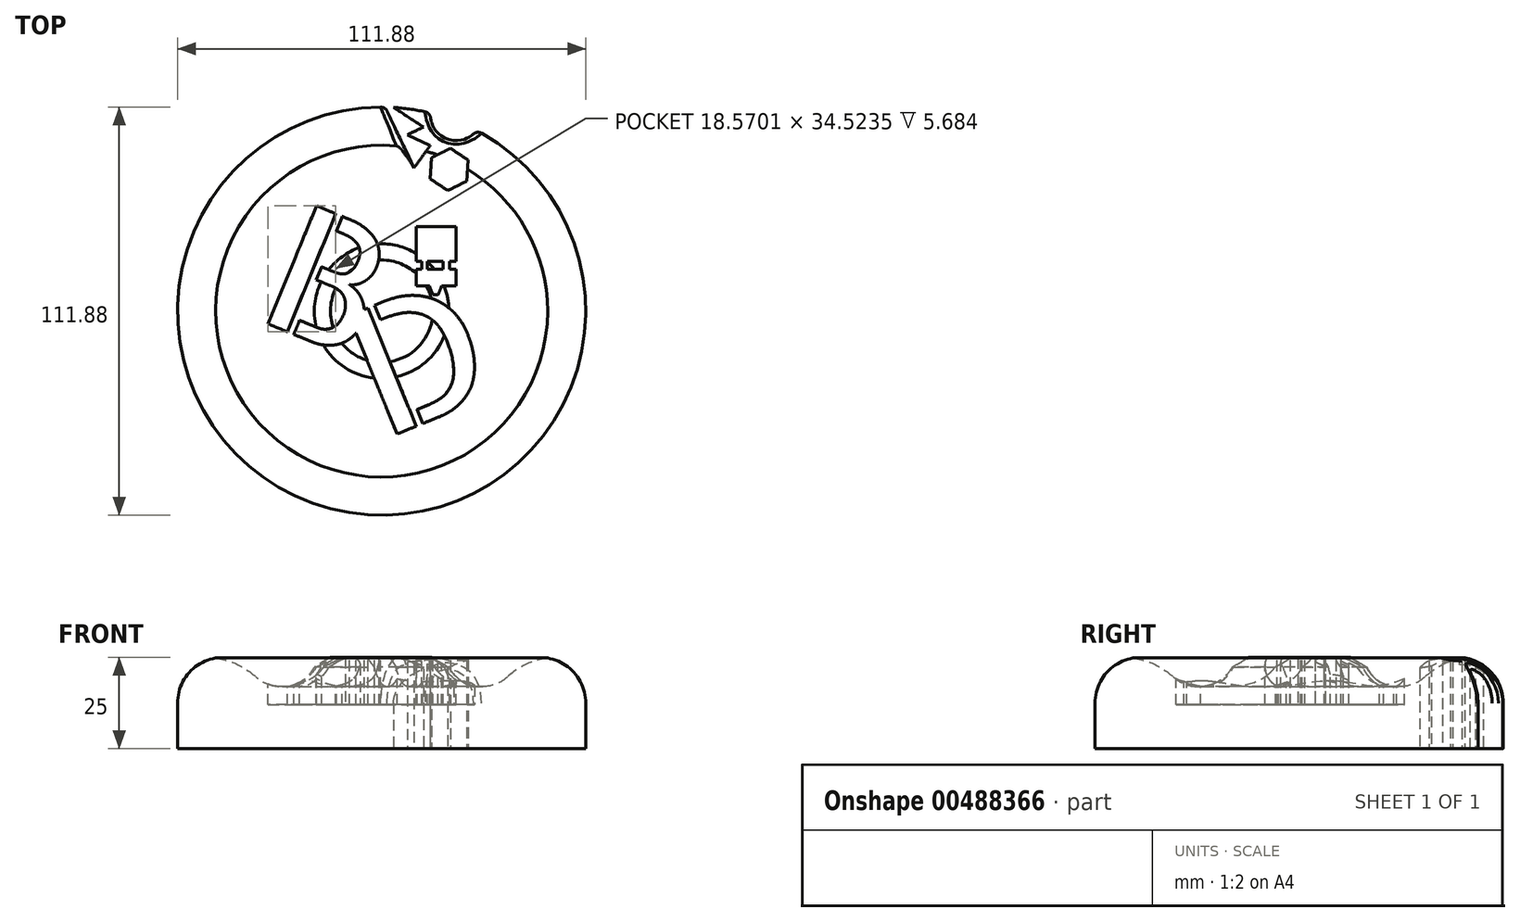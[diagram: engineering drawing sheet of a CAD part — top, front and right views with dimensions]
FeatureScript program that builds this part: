
annotation { "Feature Type Name" : "Feature", "Feature Type Description" : "" }
export const myFeature = defineFeature(function(context is Context, id is Id, definition is map)
    precondition{}
    {
        {
            var Q0;
            Q0=qCreatedBy(makeId("Top.planeOp"),FACE);
            var sketch = newSketch(context, id + "F0", { "sketchPlane" : qUnion([Q0])});
            skCircle(sketch, "E0", {"center": v(0, 0) * mm, "radius": 55.94 * mm});
            skSolve(sketch);
        }
        {
            var Q0;
            Q0 = qSketchRegion(id + "F0", true);
            extrude(context, id + "F1", {"entities" : qUnion([Q0]), "depth" : 25 * mm});
        }
        {
            var Q0;
            Q0=makeQuery(id+"F1.opExtrude","CAP_EDGE",EDGE,{"disambiguationData":[OSD([sQuery(id+"F0.wireOp",EDGE,"E0")])],"isStart":false});
            fillet(context, id + "F2", {"entities" : qUnion([Q0]), "radius" : 12.5 * mm, "tangentPropagation" : true, "allowEdgeOverflow" : false});
        }
        {
            var Q0;
            Q0=qCreatedBy(makeId("Top.planeOp"),FACE);
            var sketch = newSketch(context, id + "F3", { "sketchPlane" : qUnion([Q0])});
            skCircle(sketch, "E1", {"center": v(20.4, 53.76) * mm, "radius": 7 * mm});
            skSolve(sketch);
        }
        {
            var Q0;
            Q0=makeQuery(id+"F3.imprint","IMPRINT",FACE,{"disambiguationData":[TD([[makeQuery(id+"F3.imprint","IMPRINT",EDGE,{"derivedFrom":sQuery(id+"F3.wireOp",EDGE,"E1")}),1.0]])]});
            extrude(context, id + "F4", {"entities" : qUnion([Q0]), "operationType" : NewBodyOperationType.REMOVE, "depth" : 25 * mm});
        }
        {
            var Q0;
            Q0=qCreatedBy(makeId("Top.planeOp"),FACE);
            var sketch = newSketch(context, id + "F5", { "sketchPlane" : qUnion([Q0])});
            skLineSegment(sketch, "E2", {"start": v(0, 58) * mm, "end": v(8.89, 39.29) * mm});
            skLineSegment(sketch, "E3", {"start": v(8.89, 39.29) * mm, "end": v(13.3, 45.4) * mm});
            skLineSegment(sketch, "E4", {"start": v(13.3, 45.4) * mm, "end": v(7.07, 48.39) * mm});
            skLineSegment(sketch, "E5", {"start": v(7.07, 48.39) * mm, "end": v(11.47, 50.48) * mm});
            skLineSegment(sketch, "E6", {"start": v(11.47, 50.48) * mm, "end": v(0, 58) * mm});
            skLineSegment(sketch, "E7.0", {"start": v(13.66, 42.07) * mm, "end": v(18.86, 44.65) * mm});
            skLineSegment(sketch, "E7.1", {"start": v(18.86, 44.65) * mm, "end": v(23.7, 41.44) * mm});
            skLineSegment(sketch, "E7.2", {"start": v(23.7, 41.44) * mm, "end": v(23.33, 35.65) * mm});
            skLineSegment(sketch, "E7.3", {"start": v(23.33, 35.65) * mm, "end": v(18.14, 33.07) * mm});
            skLineSegment(sketch, "E7.4", {"start": v(18.14, 33.07) * mm, "end": v(13.3, 36.28) * mm});
            skLineSegment(sketch, "E7.5", {"start": v(13.3, 36.28) * mm, "end": v(13.66, 42.07) * mm});
            skPoint(sketch, "E7.0.midPoint", {"position": v(16.26, 43.36) * mm});
            skSolve(sketch);
        }
        {
            var Q0;
            Q0 = qSketchRegion(id + "F5", true);
            extrude(context, id + "F6", {"entities" : qUnion([Q0]), "operationType" : NewBodyOperationType.REMOVE, "depth" : 25 * mm});
        }
        {
            var Q0;
            {var subQ0=sQuery(id+"F0.wireOp",EDGE,"E0");Q0=makeQuery(id+"F4.boolean.opBoolean","INTERSECT",EDGE,{"derivedFrom":[makeQuery(id+"F8unwX3rbQihtJl_1.1.F6.boolean.opBoolean","SPLIT",FACE,{"disambiguationData":[TD([makeQuery(id+"F6.boolean.opBoolean","COPY",FACE,{"derivedFrom":makeQuery(id+"F6.opExtrude","SWEPT_FACE",FACE,{"disambiguationData":[OSD([sQuery(id+"F5.wireOp",EDGE,"E3")])]})})])],"derivedFrom":makeQuery(id+"F2.opFillet","BLEND_FACE",FACE,{"disambiguationData":[OSD([subQ0])]})}),makeQuery(id+"F4.opExtrude","SWEPT_FACE",FACE,{"disambiguationData":[OSD([sQuery(id+"F3.wireOp",EDGE,"E1")])]})]});}
            var Q1;
            Q1=makeQuery(id+"F6.boolean.opBoolean","INTERSECT",EDGE,{"derivedFrom":[makeQuery(id+"F2.opFillet","BLEND_FACE",FACE,{"disambiguationData":[OSD([sQuery(id+"F0.wireOp",EDGE,"E0")])]}),makeQuery(id+"F6.opExtrude","SWEPT_FACE",FACE,{"disambiguationData":[OSD([sQuery(id+"F5.wireOp",EDGE,"E2")])]})]});
            fillet(context, id + "F7", {"entities" : qUnion([Q0, Q1]), "radius" : 2 * mm, "tangentPropagation" : true, "allowEdgeOverflow" : false});
        }
        {
            var Q0;
            Q0=qCreatedBy(makeId("Front.planeOp"),FACE);
            var sketch = newSketch(context, id + "F8", { "sketchPlane" : qUnion([Q0])});
            skLineSegment(sketch, "E8", {"start": v(0, 28.58) * mm, "end": v(0, -4.87) * mm});
            skSolve(sketch);
        }
        {
            var Q0;
            Q0=makeQuery(id+"F1.opExtrude","CAP_FACE",FACE,{"disambiguationData":[OSD([sQuery(id+"F0.wireOp",EDGE,"E0")])],"isStart":false});
            var sketch = newSketch(context, id + "F9", { "sketchPlane" : qUnion([Q0])});
            skCircle(sketch, "E9", {"center": v(0, 0) * mm, "radius": 37.5 * mm});
            skCircle(sketch, "E10", {"center": v(0, 0) * mm, "radius": 17.5 * mm});
            skSolve(sketch);
        }
        {
            var Q0;
            {var subQ0=sQuery(id+"F5.wireOp",EDGE,"E3");var subQ8=sQuery(id+"F9.wireOp",EDGE,"E9");var subQ10=makeQuery(id+"F8unwX3rbQihtJl_1.1.F6.boolean.opBoolean","COPY",EDGE,{"derivedFrom":makeQuery(id+"F8unwX3rbQihtJl_1.1.F6.opExtrude","CAP_EDGE",EDGE,{"disambiguationData":[OSD([subQ0])],"isStart":false})});var subQ13=makeQuery(id+"F9.imprint","INTERSECT",VERTEX,{"derivedFrom":[subQ10,subQ8]});Q0=makeQuery(id+"F9.imprint","IMPRINT",FACE,{"disambiguationData":[TD([[makeQuery(id+"F9.imprint","IMPRINT",EDGE,{"disambiguationData":[TD([[subQ13,1.0]])],"derivedFrom":subQ8}),1.0]])]});}
            extrude(context, id + "F10", {"entities" : qUnion([Q0]), "operationType" : NewBodyOperationType.REMOVE, "oppositeDirection" : true, "depth" : 8 * mm});
        }
        {
            var Q0;
            Q0=makeQuery(id+"F10.boolean.opBoolean","COPY",EDGE,{"derivedFrom":makeQuery(id+"F10.opExtrude","CAP_EDGE",EDGE,{"disambiguationData":[OSD([sQuery(id+"F9.wireOp",EDGE,"E9")])],"isStart":false})});
            var Q1;
            Q1=makeQuery(id+"F10.boolean.opBoolean","COPY",EDGE,{"derivedFrom":makeQuery(id+"F10.opExtrude","CAP_EDGE",EDGE,{"disambiguationData":[OSD([sQuery(id+"F9.wireOp",EDGE,"E10")])],"isStart":false})});
            fillet(context, id + "F11", {"entities" : qUnion([Q0, Q1]), "radius" : 10 * mm, "tangentPropagation" : true, "allowEdgeOverflow" : false});
        }
        {
            var Q0;
            {var subQ0=sQuery(id+"F9.wireOp",EDGE,"E10");Q0=makeQuery(id+"F11.opFillet","BLEND_EDGE",EDGE,{"blendedFrom":[makeQuery(id+"F10.boolean.opBoolean","COPY",EDGE,{"derivedFrom":makeQuery(id+"F10.opExtrude","CAP_EDGE",EDGE,{"disambiguationData":[OSD([subQ0])],"isStart":false})}),makeQuery(id+"F10.boolean.opBoolean","SPLIT",FACE,{"disambiguationData":[TD([makeQuery(id+"F10.opExtrude","SWEPT_FACE",FACE,{"disambiguationData":[OSD([subQ0])]})])],"derivedFrom":makeQuery(id+"F1.opExtrude","CAP_FACE",FACE,{"disambiguationData":[OSD([sQuery(id+"F0.wireOp",EDGE,"E0")])],"isStart":false})})],"blendedInto":[makeQuery(id+"F10.boolean.opBoolean","SPLIT",FACE,{"disambiguationData":[TD([makeQuery(id+"F10.opExtrude","SWEPT_FACE",FACE,{"disambiguationData":[OSD([subQ0])]})])],"derivedFrom":makeQuery(id+"F1.opExtrude","CAP_FACE",FACE,{"disambiguationData":[OSD([sQuery(id+"F0.wireOp",EDGE,"E0")])],"isStart":false})})]});}
            chamfer(context, id + "F12", {"entities" : qUnion([Q0]), "width" : 5 * mm, "tangentPropagation" : true});
        }
        {
            var Q0;
            Q0=qCreatedBy(makeId("Top.planeOp"),FACE);
            cPlane(context, id + "F13", {"entities" : qUnion([Q0]), "cplaneType" : CPlaneType.OFFSET, "offset" : 25 * mm, "width" : 150 * mm, "height" : 150 * mm});
        }
        {
            var Q0;
            Q0=qCreatedBy(id+"F13.planeOp",FACE);
            var sketch = newSketch(context, id + "F14", { "sketchPlane" : qUnion([Q0])});
            skText(sketch, "E11", { "text": "B", "fontName": "AllertaStencil-Regular.ttf"});
            skText(sketch, "E12", { "text": "D", "fontName": "AllertaStencil-Regular.ttf"});
            skLineSegment(sketch, "E13.bottom", {"start": v(9.47, 23.24) * mm, "end": v(20.36, 23.24) * mm});
            skLineSegment(sketch, "E13.top", {"start": v(9.47, 13.6) * mm, "end": v(20.36, 13.6) * mm});
            skLineSegment(sketch, "E13.left", {"start": v(9.47, 23.24) * mm, "end": v(9.47, 13.6) * mm});
            skLineSegment(sketch, "E13.right", {"start": v(20.36, 23.24) * mm, "end": v(20.36, 13.6) * mm});
            skLineSegment(sketch, "E14.bottom", {"start": v(9.47, 11.46) * mm, "end": v(20.36, 11.46) * mm});
            skLineSegment(sketch, "E14.top", {"start": v(9.47, 6.9) * mm, "end": v(20.36, 6.9) * mm});
            skLineSegment(sketch, "E14.left", {"start": v(9.47, 11.46) * mm, "end": v(9.47, 6.9) * mm});
            skLineSegment(sketch, "E14.right", {"start": v(20.36, 11.46) * mm, "end": v(20.36, 6.9) * mm});
            skLineSegment(sketch, "E15.bottom", {"start": v(10.96, 13.6) * mm, "end": v(12.5, 13.6) * mm});
            skLineSegment(sketch, "E15.top", {"start": v(10.96, 11.46) * mm, "end": v(12.5, 11.46) * mm});
            skLineSegment(sketch, "E15.left", {"start": v(10.96, 13.6) * mm, "end": v(10.96, 11.46) * mm});
            skLineSegment(sketch, "E15.right", {"start": v(12.5, 13.6) * mm, "end": v(12.5, 11.46) * mm});
            skLineSegment(sketch, "E16.bottom", {"start": v(18.58, 13.6) * mm, "end": v(16.83, 13.6) * mm});
            skLineSegment(sketch, "E16.top", {"start": v(18.58, 11.46) * mm, "end": v(16.83, 11.46) * mm});
            skLineSegment(sketch, "E16.left", {"start": v(18.58, 13.6) * mm, "end": v(18.58, 11.46) * mm});
            skLineSegment(sketch, "E16.right", {"start": v(16.83, 13.6) * mm, "end": v(16.83, 11.46) * mm});
            skLineSegment(sketch, "E17", {"start": v(13.1, 6.9) * mm, "end": v(14.07, 4.5) * mm});
            skLineSegment(sketch, "E18", {"start": v(14.07, 4.5) * mm, "end": v(15.5, 4.5) * mm});
            skLineSegment(sketch, "E19", {"start": v(15.5, 4.5) * mm, "end": v(16.48, 6.9) * mm});
            const initialGuessF14  = {"E11": [-0.03536, -0.00174, 0.9249, -0.3802, 0.035], "E12": [0, -0.0354, 0.92596, 0.37761, 0.035]};
            skSetInitialGuess(sketch, initialGuessF14);
            skSolve(sketch);
        }
        {
            var Q0;
            Q0 = qSketchRegion(id + "F14", true);
            var Q1;
            {var subQ0=sQuery(id+"F14.wireOp",EDGE,"E14.left");Q1=makeQuery(id+"F14.imprint","IMPRINT",FACE,{"disambiguationData":[TD([[makeQuery(id+"F14.imprint","IMPRINT",EDGE,{"derivedFrom":subQ0}),1.0]])]});}
            var Q2;
            Q2=makeQuery(id+"F14.imprint","IMPRINT",FACE,{"disambiguationData":[TD([[makeQuery(id+"F14.imprint","IMPRINT",EDGE,{"derivedFrom":sQuery(id+"F14.wireOp",EDGE,"E13.bottom")}),-1.0]])]});
            var Q3;
            Q3=makeQuery(id+"F14.imprint","IMPRINT",FACE,{"disambiguationData":[TD([[makeQuery(id+"F14.imprint","IMPRINT",EDGE,{"derivedFrom":sQuery(id+"F14.wireOp",EDGE,"E16.bottom")}),1.0]])]});
            var Q4;
            Q4=makeQuery(id+"F14.imprint","IMPRINT",FACE,{"disambiguationData":[TD([[makeQuery(id+"F14.imprint","IMPRINT",EDGE,{"derivedFrom":sQuery(id+"F14.wireOp",EDGE,"E15.bottom")}),-1.0]])]});
            extrude(context, id + "F15", {"entities" : qUnion([Q0, Q1, Q2, Q3, Q4]), "operationType" : NewBodyOperationType.REMOVE, "oppositeDirection" : true, "depth" : 13 * mm});
        }
        {
            var Q0;
            {var subQ8=sQuery(id+"F0.wireOp",EDGE,"E0");var subQ13=makeQuery(id+"F2.opFillet","BLEND_FACE",FACE,{"disambiguationData":[OSD([subQ8])]});var subQ17=makeQuery(id+"F1.opExtrude","CAP_FACE",FACE,{"disambiguationData":[OSD([subQ8])],"isStart":false});var subQ46=sQuery(id+"F9.wireOp",EDGE,"E9");Q0=makeQuery(id+"F11.opFillet","BLEND_EDGE",EDGE,{"blendedFrom":[makeQuery(id+"F10.boolean.opBoolean","COPY",EDGE,{"derivedFrom":makeQuery(id+"F10.opExtrude","CAP_EDGE",EDGE,{"disambiguationData":[OSD([subQ46])],"isStart":false})}),makeQuery(id+"F10.boolean.opBoolean","SPLIT",FACE,{"disambiguationData":[TD([subQ13])],"derivedFrom":subQ17})],"blendedInto":[makeQuery(id+"F10.boolean.opBoolean","SPLIT",FACE,{"disambiguationData":[TD([subQ13])],"derivedFrom":subQ17})]});}
            fillet(context, id + "F16", {"entities" : qUnion([Q0]), "radius" : 20 * mm, "tangentPropagation" : true, "allowEdgeOverflow" : false});
        }
    });
